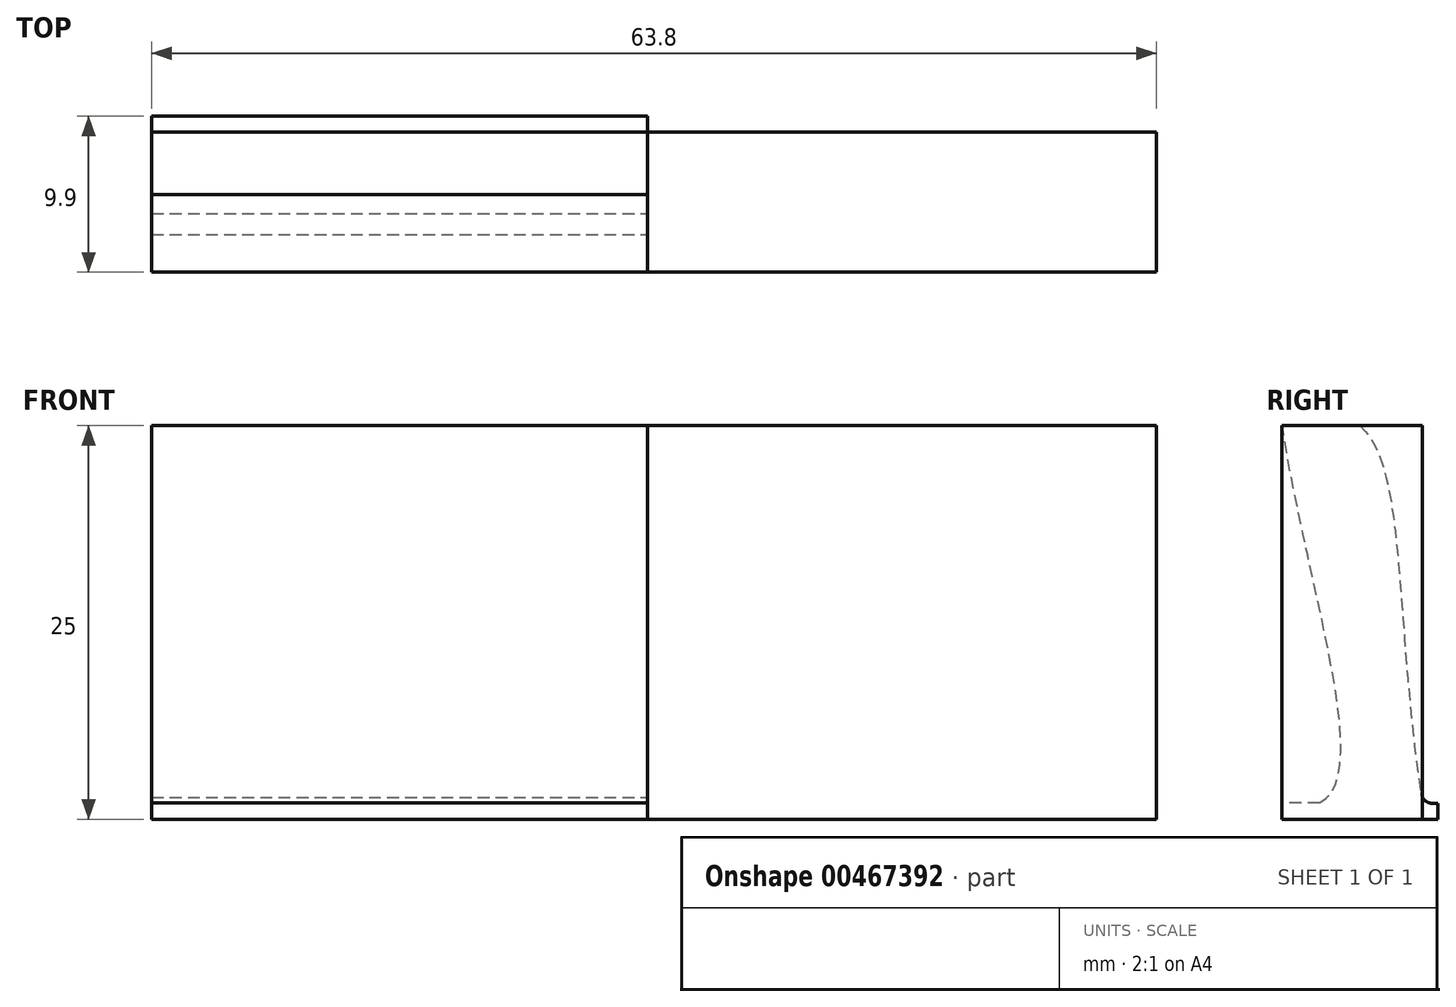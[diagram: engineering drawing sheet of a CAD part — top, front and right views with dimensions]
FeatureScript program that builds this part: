
annotation { "Feature Type Name" : "Feature", "Feature Type Description" : "" }
export const myFeature = defineFeature(function(context is Context, id is Id, definition is map)
    precondition{}
    {
        {
            var Q0;
            Q0=qCreatedBy(makeId("Top.planeOp"),FACE);
            var sketch = newSketch(context, id + "F0", { "sketchPlane" : qUnion([Q0])});
            skLineSegment(sketch, "E0.bottom", {"start": v(-10.68, 3.85) * mm, "end": v(21.62, 3.85) * mm});
            skLineSegment(sketch, "E0.top", {"start": v(-10.68, -5.05) * mm, "end": v(21.62, -5.05) * mm});
            skLineSegment(sketch, "E0.left", {"start": v(-10.68, 3.85) * mm, "end": v(-10.68, -5.05) * mm});
            skLineSegment(sketch, "E0.right", {"start": v(21.62, 3.85) * mm, "end": v(21.62, -5.05) * mm});
            skSolve(sketch);
        }
        {
            var Q0;
            Q0 = qSketchRegion(id + "F0", true);
            extrude(context, id + "F1", {"entities" : qUnion([Q0]), "depth" : 25 * mm});
        }
        {
            var Q0;
            Q0=makeQuery(id+"F1.opExtrude","SWEPT_FACE",FACE,{"disambiguationData":[OSD([sQuery(id+"F0.wireOp",EDGE,"E0.left")])]});
            var sketch = newSketch(context, id + "F2", { "sketchPlane" : qUnion([Q0])});
            skPoint(sketch, "E1.newPointA", {"position": v(5.05, 1.04) * mm});
            skPoint(sketch, "E1.newPointB", {"position": v(5.05, 0) * mm});
            skFitSpline(sketch, "E2", {"points": [v(2.68, 1.04) * mm, v(5.05, 25) * mm], "startDerivative": vector(-10.56, 5.06) * mm, "endDerivative": vector(4.83, 31.11) * mm});
            skLineSegment(sketch, "E3", {"start": v(-3.85, 0) * mm, "end": v(-4.85, 0) * mm});
            skLineSegment(sketch, "E4", {"start": v(-4.85, 0) * mm, "end": v(-4.85, 1) * mm});
            skLineSegment(sketch, "E5", {"start": v(-4.85, 1) * mm, "end": v(-4.54, 1) * mm});
            skFitSpline(sketch, "E6", {"points": [v(5.05, 25) * mm, v(-3.85, 1) * mm], "startDerivative": vector(-26.7, 11.19) * mm, "endDerivative": vector(-7.4, -48.77) * mm});
            skLineSegment(sketch, "E7", {"start": v(-3.85, 0) * mm, "end": v(-2.4, 0) * mm});
            skArc(sketch, "E8.filletArc", {"start": v(-4.54, 1) * mm, "mid": v(-4.01, 1.2) * mm, "end": v(-3.75, 1.69) * mm});
            skLineSegment(sketch, "E9", {"start": v(2.68, 1.04) * mm, "end": v(5.05, 1.04) * mm});
            skLineSegment(sketch, "E10", {"start": v(5.05, 0) * mm, "end": v(5.05, 1.04) * mm});
            skLineSegment(sketch, "E11.0", {"start": v(-4.85, -1) * mm, "end": v(-4.54, -1) * mm});
            skArc(sketch, "E11.1", {"start": v(-4.54, -1) * mm, "mid": v(-2.7, -0.32) * mm, "end": v(-1.77, 1.4) * mm});
            skFitSpline(sketch, "E11.2", {"points": [v(4.28, 23.16) * mm, v(3.8, 23.36) * mm, v(2.96, 23.63) * mm, v(2.26, 23.72) * mm, v(1.9, 23.7) * mm, v(1.72, 23.65) * mm, v(1.59, 23.6) * mm, v(1.47, 23.52) * mm, v(1.33, 23.4) * mm, v(1.12, 23.15) * mm, v(0.81, 22.6) * mm, v(0.45, 21.57) * mm, v(0.15, 20.19) * mm, v(-0.1, 18.51) * mm, v(-0.38, 15.93) * mm, v(-0.66, 12.1) * mm, v(-1.08, 6.76) * mm, v(-1.55, 2.77) * mm, v(-1.87, 0.7) * mm]});
            skFitSpline(sketch, "E11.3", {"points": [v(1.81, -0.77) * mm, v(1.58, -0.66) * mm, v(1.14, -0.39) * mm, v(0.59, 0.13) * mm, v(0.16, 0.72) * mm, v(-0.26, 1.54) * mm, v(-0.55, 2.6) * mm, v(-0.69, 3.93) * mm, v(-0.67, 5.33) * mm, v(-0.55, 6.83) * mm, v(-0.33, 8.43) * mm, v(0.06, 10.68) * mm, v(0.7, 13.7) * mm, v(1.56, 17.53) * mm, v(2.4, 21.46) * mm, v(2.88, 24.05) * mm, v(3.08, 25.3) * mm]});
            skLineSegment(sketch, "E12", {"start": v(0.74, 0) * mm, "end": v(5.05, 0) * mm});
            skLineSegment(sketch, "E13", {"start": v(-2.4, 0) * mm, "end": v(0.74, 0) * mm});
            skSolve(sketch);
        }
        {
            var Q0;
            {var subQ10=sQuery(id+"F2.wireOp",EDGE,"E6");Q0=makeQuery(id+"F2.imprint","IMPRINT",FACE,{"disambiguationData":[TD([[makeQuery(id+"F2.imprint","IMPRINT",EDGE,{"derivedFrom":subQ10}),1.0]])]});}
            var Q1;
            {var subQ4=sQuery(id+"F2.wireOp",EDGE,"E3");Q1=makeQuery(id+"F2.imprint","IMPRINT",FACE,{"disambiguationData":[TD([[makeQuery(id+"F2.imprint","IMPRINT",EDGE,{"derivedFrom":subQ4}),-1.0]])]});}
            var Q2;
            {var subQ1=sQuery(id+"F2.wireOp",EDGE,"d4131d25-7f19-45c8-a7df-d10e1ed95825.3");Q2=makeQuery(id+"F2.imprint","IMPRINT",FACE,{"disambiguationData":[TD([[makeQuery(id+"F2.imprint","IMPRINT",EDGE,{"derivedFrom":subQ1}),1.0]])]});}
            var Q3;
            {var subQ4=sQuery(id+"F2.wireOp",EDGE,"IYSaOSWp-P1SS-6KTv-ztrQ-2KVvS2knigyJ");Q3=makeQuery(id+"F2.imprint","IMPRINT",FACE,{"disambiguationData":[TD([[makeQuery(id+"F2.imprint","IMPRINT",EDGE,{"derivedFrom":subQ4}),1.0]])]});}
            var Q4;
            {var subQ0=sQuery(id+"F2.wireOp",EDGE,"E2");Q4=makeQuery(id+"F2.imprint","IMPRINT",FACE,{"disambiguationData":[TD([[makeQuery(id+"F2.imprint","IMPRINT",EDGE,{"derivedFrom":subQ0}),1.0]])]});}
            extrude(context, id + "F3", {"entities" : qUnion([Q0, Q1, Q2, Q3, Q4]), "depth" : 31.5 * mm});
        }
    });
